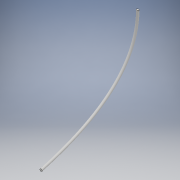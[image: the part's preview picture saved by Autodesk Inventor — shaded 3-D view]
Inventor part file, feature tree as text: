
AUTODESK INVENTOR PART (.ipt)
format: ipt  version: 2018 (Build 220112000, 112)  size: 156,672 bytes
history: native  units: mm
features: sketch x3, sweep x1, extrude x1, plane x1
ambient origin geometry x8: Origin, YZ Plane, XZ Plane, XY Plane, X Axis, Y Axis, Z Axis, Center Point
bodies: Solid1 (feature_tree)
feature tree (6):
  sweep  "Sweep1"
  extrude  "Extrusion1"  Depth=350.0mm
  plane  "Work Plane1"
  sketch  "Sketch1"  dims[d1=750.0mm d3=400.0mm]
  sketch  "Sketch3"  dims[d4=150.0mm d5=350.0mm]
  sketch  "Sketch4"  dims[d6=20.0mm d7=0.0mm d8=0.0mm d9=2.0mm d10=5.0mm d12=10.0mm d13=20.0mm d14=0.0mm d15=3.0mm]
